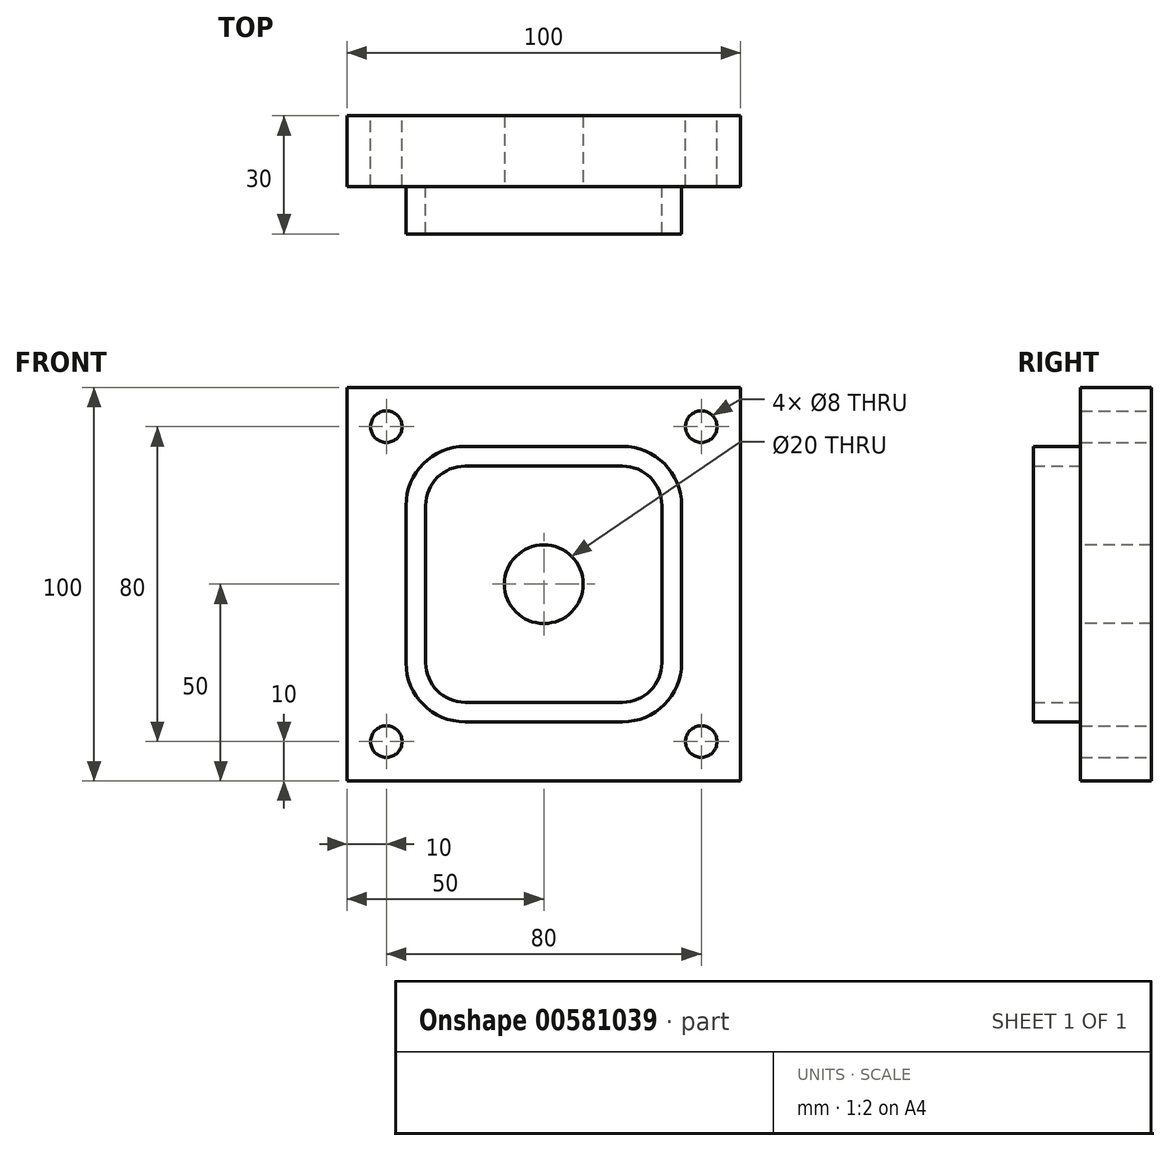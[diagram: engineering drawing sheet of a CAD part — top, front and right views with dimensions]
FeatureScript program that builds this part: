
annotation { "Feature Type Name" : "Feature", "Feature Type Description" : "" }
export const myFeature = defineFeature(function(context is Context, id is Id, definition is map)
    precondition{}
    {
        {
            var Q0;
            Q0=qCreatedBy(makeId("Front.planeOp"),FACE);
            var sketch = newSketch(context, id + "F0", { "sketchPlane" : qUnion([Q0])});
            skLineSegment(sketch, "E0.bottom", {"start": v(-50, 50) * mm, "end": v(50, 50) * mm});
            skLineSegment(sketch, "E0.top", {"start": v(-50, -50) * mm, "end": v(50, -50) * mm});
            skLineSegment(sketch, "E0.left", {"start": v(-50, 50) * mm, "end": v(-50, -50) * mm});
            skLineSegment(sketch, "E0.right", {"start": v(50, 50) * mm, "end": v(50, -50) * mm});
            skPoint(sketch, "E0.middle", {"position": v(0, 0) * mm});
            skCircle(sketch, "E1", {"center": v(-40, 40) * mm, "radius": 4 * mm});
            skLineSegment(sketch, "E2.bottom", {"start": v(-40, 40) * mm, "end": v(40, 40) * mm, "construction": true});
            skLineSegment(sketch, "E2.top", {"start": v(-40, -40) * mm, "end": v(40, -40) * mm, "construction": true});
            skLineSegment(sketch, "E2.left", {"start": v(-40, 40) * mm, "end": v(-40, -40) * mm, "construction": true});
            skLineSegment(sketch, "E2.right", {"start": v(40, 40) * mm, "end": v(40, -40) * mm, "construction": true});
            skCircle(sketch, "E3", {"center": v(40, 40) * mm, "radius": 4 * mm});
            skCircle(sketch, "E4", {"center": v(40, -40) * mm, "radius": 4 * mm});
            skCircle(sketch, "E5", {"center": v(-40, -40) * mm, "radius": 4 * mm});
            skSolve(sketch);
        }
        {
            var Q0;
            Q0=makeQuery(id+"F0.imprint","IMPRINT",FACE,{"disambiguationData":[TD([[makeQuery(id+"F0.imprint","IMPRINT",EDGE,{"derivedFrom":sQuery(id+"F0.wireOp",EDGE,"E0.bottom")}),-1.0]])]});
            extrude(context, id + "F1", {"entities" : qUnion([Q0]), "depth" : 18 * mm, "offsetDistance" : 25 * mm});
        }
        {
            var Q0;
            Q0=makeQuery(id+"F1.opExtrude","CAP_FACE",FACE,{"disambiguationData":[OSD([sQuery(id+"F0.wireOp",EDGE,"E0.bottom"),sQuery(id+"F0.wireOp",EDGE,"E0.top"),sQuery(id+"F0.wireOp",EDGE,"E0.left"),sQuery(id+"F0.wireOp",EDGE,"E0.right"),sQuery(id+"F0.wireOp",EDGE,"E1"),sQuery(id+"F0.wireOp",EDGE,"E3"),sQuery(id+"F0.wireOp",EDGE,"E4"),sQuery(id+"F0.wireOp",EDGE,"E5")])],"isStart":false});
            var sketch = newSketch(context, id + "F2", { "sketchPlane" : qUnion([Q0])});
            skLineSegment(sketch, "E6.bottom", {"start": v(-20, 35) * mm, "end": v(20, 35) * mm});
            skLineSegment(sketch, "E6.top", {"start": v(-20, -35) * mm, "end": v(20, -35) * mm});
            skLineSegment(sketch, "E6.left", {"start": v(-35, 20) * mm, "end": v(-35, -20) * mm});
            skLineSegment(sketch, "E6.right", {"start": v(35, 20) * mm, "end": v(35, -20) * mm});
            skPoint(sketch, "E6.middle", {"position": v(0, 0) * mm});
            skPoint(sketch, "E7.visualSharp", {"position": v(-35, 35) * mm});
            skArc(sketch, "E7.filletArc", {"start": v(-20, 35) * mm, "mid": v(-30.6, 30.6) * mm, "end": v(-35, 20) * mm});
            skPoint(sketch, "E8.visualSharp", {"position": v(-35, -35) * mm});
            skArc(sketch, "E8.filletArc", {"start": v(-35, -20) * mm, "mid": v(-30.6, -30.6) * mm, "end": v(-20, -35) * mm});
            skPoint(sketch, "E9.visualSharp", {"position": v(35, -35) * mm});
            skArc(sketch, "E9.filletArc", {"start": v(20, -35) * mm, "mid": v(30.6, -30.6) * mm, "end": v(35, -20) * mm});
            skPoint(sketch, "E10.visualSharp", {"position": v(35, 35) * mm});
            skArc(sketch, "E10.filletArc", {"start": v(35, 20) * mm, "mid": v(30.6, 30.6) * mm, "end": v(20, 35) * mm});
            skLineSegment(sketch, "E11.bottom", {"start": v(-20, 30) * mm, "end": v(20, 30) * mm});
            skLineSegment(sketch, "E11.top", {"start": v(-20, -30) * mm, "end": v(20, -30) * mm});
            skLineSegment(sketch, "E11.left", {"start": v(-30, 20) * mm, "end": v(-30, -20) * mm});
            skLineSegment(sketch, "E11.right", {"start": v(30, 20) * mm, "end": v(30, -20) * mm});
            skPoint(sketch, "E12.visualSharp", {"position": v(30, 30) * mm});
            skArc(sketch, "E12.filletArc", {"start": v(30, 20) * mm, "mid": v(27.07, 27.07) * mm, "end": v(20, 30) * mm});
            skPoint(sketch, "E13.visualSharp", {"position": v(30, -30) * mm});
            skArc(sketch, "E13.filletArc", {"start": v(20, -30) * mm, "mid": v(27.07, -27.07) * mm, "end": v(30, -20) * mm});
            skPoint(sketch, "E14.visualSharp", {"position": v(-30, -30) * mm});
            skArc(sketch, "E14.filletArc", {"start": v(-30, -20) * mm, "mid": v(-27.07, -27.07) * mm, "end": v(-20, -30) * mm});
            skPoint(sketch, "E15.visualSharp", {"position": v(-30, 30) * mm});
            skArc(sketch, "E15.filletArc", {"start": v(-20, 30) * mm, "mid": v(-27.07, 27.07) * mm, "end": v(-30, 20) * mm});
            skSolve(sketch);
        }
        {
            var Q0;
            Q0=makeQuery(id+"F2.imprint","IMPRINT",FACE,{"disambiguationData":[TD([[makeQuery(id+"F2.imprint","IMPRINT",EDGE,{"derivedFrom":sQuery(id+"F2.wireOp",EDGE,"E6.bottom")}),-1.0]])]});
            extrude(context, id + "F3", {"entities" : qUnion([Q0]), "operationType" : NewBodyOperationType.ADD, "depth" : 12 * mm, "offsetDistance" : 25 * mm});
        }
        {
            var Q0;
            Q0=makeQuery(id+"F3.boolean.opBoolean","SPLIT",FACE,{"disambiguationData":[TD([makeQuery(id+"F3.opExtrude","SWEPT_FACE",FACE,{"disambiguationData":[OSD([sQuery(id+"F2.wireOp",EDGE,"E11.bottom")])]})])],"derivedFrom":makeQuery(id+"F1.opExtrude","CAP_FACE",FACE,{"disambiguationData":[OSD([sQuery(id+"F0.wireOp",EDGE,"E0.bottom"),sQuery(id+"F0.wireOp",EDGE,"E0.top"),sQuery(id+"F0.wireOp",EDGE,"E0.left"),sQuery(id+"F0.wireOp",EDGE,"E0.right"),sQuery(id+"F0.wireOp",EDGE,"E1"),sQuery(id+"F0.wireOp",EDGE,"E3"),sQuery(id+"F0.wireOp",EDGE,"E4"),sQuery(id+"F0.wireOp",EDGE,"E5")])],"isStart":false})});
            var sketch = newSketch(context, id + "F4", { "sketchPlane" : qUnion([Q0])});
            skCircle(sketch, "E16", {"center": v(0, 0) * mm, "radius": 10 * mm});
            skSolve(sketch);
        }
        {
            var Q0;
            Q0=makeQuery(id+"F4.imprint","IMPRINT",FACE,{"disambiguationData":[TD([[makeQuery(id+"F4.imprint","IMPRINT",EDGE,{"derivedFrom":sQuery(id+"F4.wireOp",EDGE,"E16")}),1.0]])]});
            extrude(context, id + "F5", {"entities" : qUnion([Q0]), "operationType" : NewBodyOperationType.REMOVE, "oppositeDirection" : true, "depth" : 30 * mm, "offsetDistance" : 25 * mm});
        }
    });
